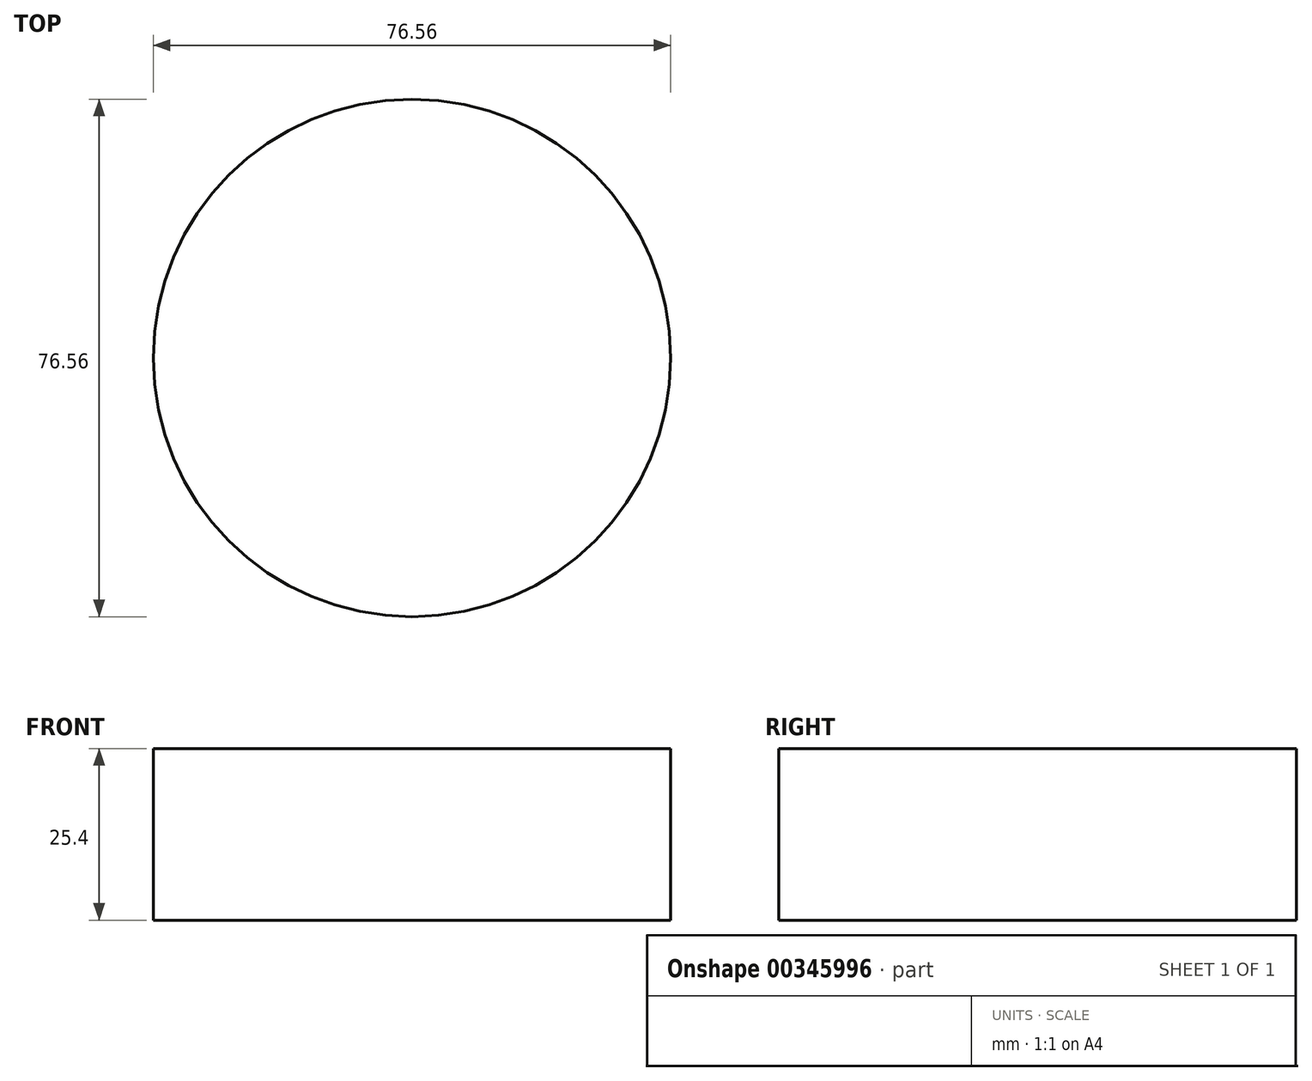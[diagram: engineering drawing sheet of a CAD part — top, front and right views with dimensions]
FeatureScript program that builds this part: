
annotation { "Feature Type Name" : "Feature", "Feature Type Description" : "" }
export const myFeature = defineFeature(function(context is Context, id is Id, definition is map)
    precondition{}
    {
        {
            var Q0;
            Q0=qCreatedBy(makeId("Top.planeOp"),FACE);
            var sketch = newSketch(context, id + "F0", { "sketchPlane" : qUnion([Q0])});
            skCircle(sketch, "E0", {"center": v(0, 0) * mm, "radius": 38.28 * mm});
            skSolve(sketch);
        }
        {
            var Q0;
            Q0=makeQuery(id+"F0.imprint","IMPRINT",FACE,{"disambiguationData":[TD([[makeQuery(id+"F0.imprint","IMPRINT",EDGE,{"derivedFrom":sQuery(id+"F0.wireOp",EDGE,"E0")}),1.0]])]});
            extrude(context, id + "F1", {"entities" : qUnion([Q0]), "depth" : 25.4 * mm});
        }
    });
